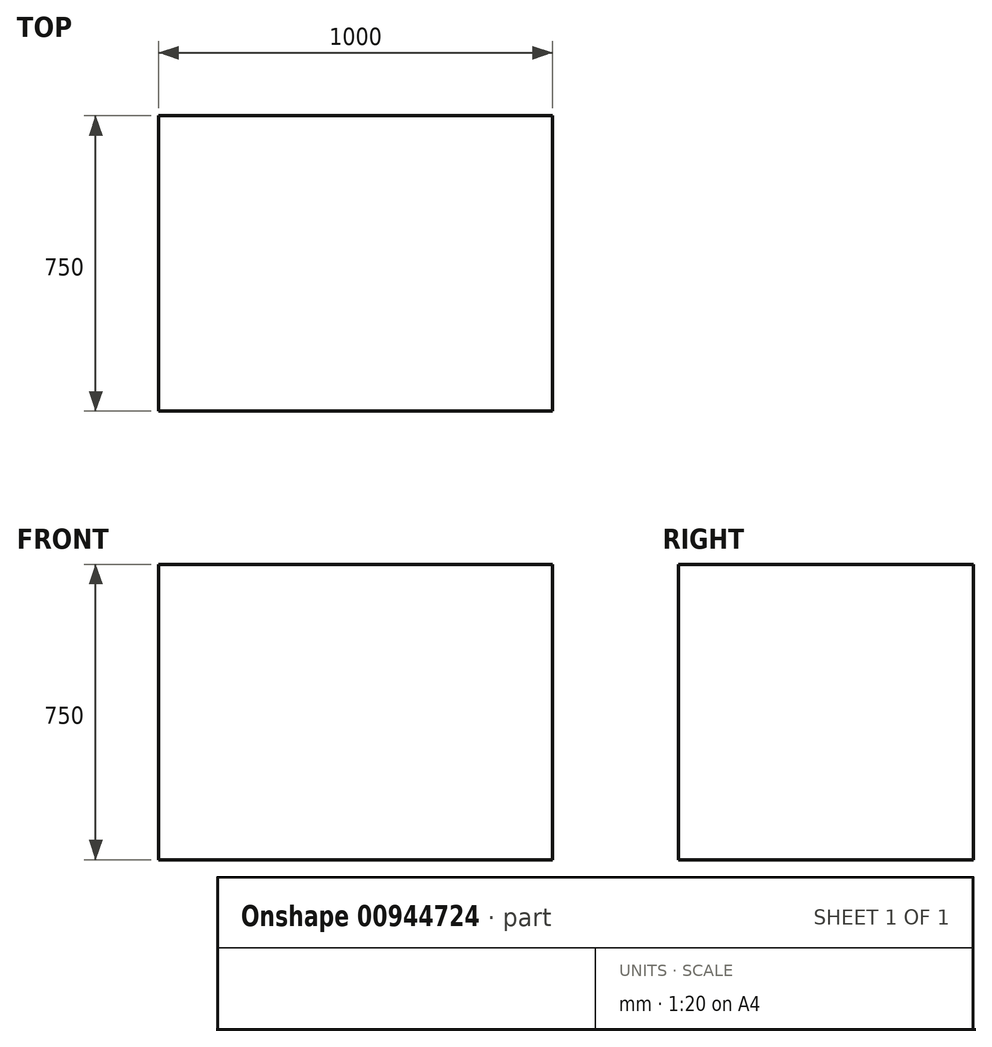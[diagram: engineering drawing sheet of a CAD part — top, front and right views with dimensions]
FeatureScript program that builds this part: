
annotation { "Feature Type Name" : "Feature", "Feature Type Description" : "" }
export const myFeature = defineFeature(function(context is Context, id is Id, definition is map)
    precondition{}
    {
        {
            var Q0;
            Q0=qCreatedBy(makeId("Top.planeOp"),FACE);
            var sketch = newSketch(context, id + "F0", { "sketchPlane" : qUnion([Q0])});
            skLineSegment(sketch, "E0.bottom", {"start": v(0, 0) * mm, "end": v(1000, 0) * mm});
            skLineSegment(sketch, "E0.top", {"start": v(0, -750) * mm, "end": v(1000, -750) * mm});
            skLineSegment(sketch, "E0.left", {"start": v(0, 0) * mm, "end": v(0, -750) * mm});
            skLineSegment(sketch, "E0.right", {"start": v(1000, 0) * mm, "end": v(1000, -750) * mm});
            skSolve(sketch);
        }
        {
            var Q0;
            Q0=makeQuery(id+"F0.imprint","IMPRINT",FACE,{"disambiguationData":[TD([[makeQuery(id+"F0.imprint","IMPRINT",EDGE,{"derivedFrom":sQuery(id+"F0.wireOp",EDGE,"E0.bottom")}),-1.0]])]});
            extrude(context, id + "F1", {"entities" : qUnion([Q0]), "depth" : 750 * mm, "offsetDistance" : 25 * mm});
        }
    });
